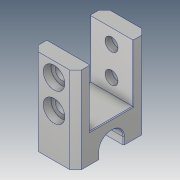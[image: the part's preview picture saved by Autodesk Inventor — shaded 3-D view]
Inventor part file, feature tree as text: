
AUTODESK INVENTOR PART (.ipt)
format: ipt  version: 2018.2 (Build 222227000, 227)  size: 208,384 bytes
history: native  units: mm
features: sketch x5, extrude x2, hole x2, projected_geometry x2, mirror x1, chamfer x1
ambient origin geometry x8: Origin, YZ Plane, XZ Plane, XY Plane, X Axis, Y Axis, Z Axis, Center Point
bodies: Volumenkörper1 (feature_tree)
feature tree (13):
  extrude  "Grundkörper"  Depth=60.0mm
  extrude  "Ausschnitt"  Depth=40.0mm
  hole  "DIN7984_M8_Boh"  [1 undecoded]
  mirror  "Spiegeln_DIN7984_M8_Boh"
  hole  "M5x10"  [1 undecoded]
  sketch  "Skizze"  dims[d19=40.0mm d20=20.0mm d21=20.0mm d22=9.0mm d23=6.0mm d24=15.0mm d25=5.4mm d26=90.0deg d27=8.0mm d28=20.594885mm d29=33.4mm d30=4.134mm d31=10.0mm d32=5.0mm d33=3.9mm d34=90.0deg d35=14.2mm d36=20.594885mm d37=4.0mm d38=2.0mm d39=45.0deg d40=0.5mm d41=2.0mm d42=45.0deg]
  chamfer  "Fase_Allgemein"  Distance=40.0mm
  sketch  "Skizze1"  dims[d0=50.0mm d1=60.0mm]
  sketch  "Skizze2"  dims[d2=30.0mm d3=0.0mm d4=40.0mm]
  sketch  "Skizze4"  dims[d5=30.0mm d14=13.0mm]
  sketch  "Skizze5"  dims[d15=16.8mm d16=8.0mm d17=40.0mm d18=0.0mm]
  projected_geometry  "Projizierte Kontur1"
  projected_geometry  "Projizierte Kontur2"
note: 2 required parameter values undecoded (feature->parameter linkage not recoverable at this tier; creation-order binding heuristic only, values carry confidence <= 0.55)
